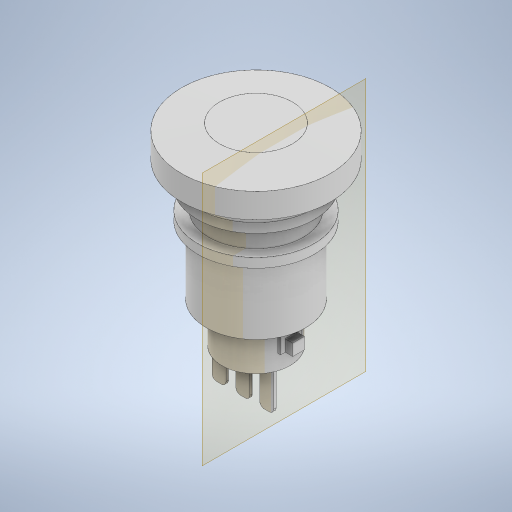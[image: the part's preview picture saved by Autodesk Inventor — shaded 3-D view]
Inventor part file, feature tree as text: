
AUTODESK INVENTOR PART (.ipt)
format: ipt  version: 2023 (Build 270158000, 158)  size: 360,448 bytes
history: native  units: in
note: dims shown in document units (in); Inventor stores cm internally (conversion verified against a paired STEP export)
features: sketch x4, extrude x3, revolve x1, fillet x1, plane x1
ambient origin geometry x8: Origin, YZ Plane, XZ Plane, XY Plane, X Axis, Y Axis, Z Axis, Center Point
bodies: Solid1 (feature_tree)
feature tree (10):
  revolve  "Revolution1"  [1 undecoded]
  extrude  "Extrusion1"  Depth=0.9783in
  fillet  "Fillet1"  Radius=0.5748in
  plane  "Work Plane1"
  extrude  "Extrusion2"  Depth=0.0787in
  extrude  "Extrusion3"  Depth=0.1772in
  sketch  "Sketch1"  dims[d2=1.252in d3=0.9843in]
  sketch  "Sketch2"  dims[d5=0.7953in d6=0.9783in d9=0.5748in]
  sketch  "Sketch3"  dims[d10=0.3425in d13=0.0787in]
  sketch  "Sketch4"  dims[d14=0.1772in d15=0.1772in d16=0.0787in d17=0.2067in d18=90.0deg d19=0.8386in d20=0.5689in d21=0.6122in d22=0.3248in d23=0.0197in d24=0.1181in d25=0.0827in d26=0.0827in d29=0.5748in d31=0.1102in d32=0.0591in d33=0.315in d34=0.0in d35=0.0394in d36=0.2362in d37=0.1772in d38=0.2165in d39=0.0886in d40=0.0591in d41=0.0in d42=0.0984in d43=0.0984in d44=0.0492in d45=0.063in d46=0.0in]
note: 1 required parameter value undecoded (feature->parameter linkage not recoverable at this tier; creation-order binding heuristic only, values carry confidence <= 0.55)
